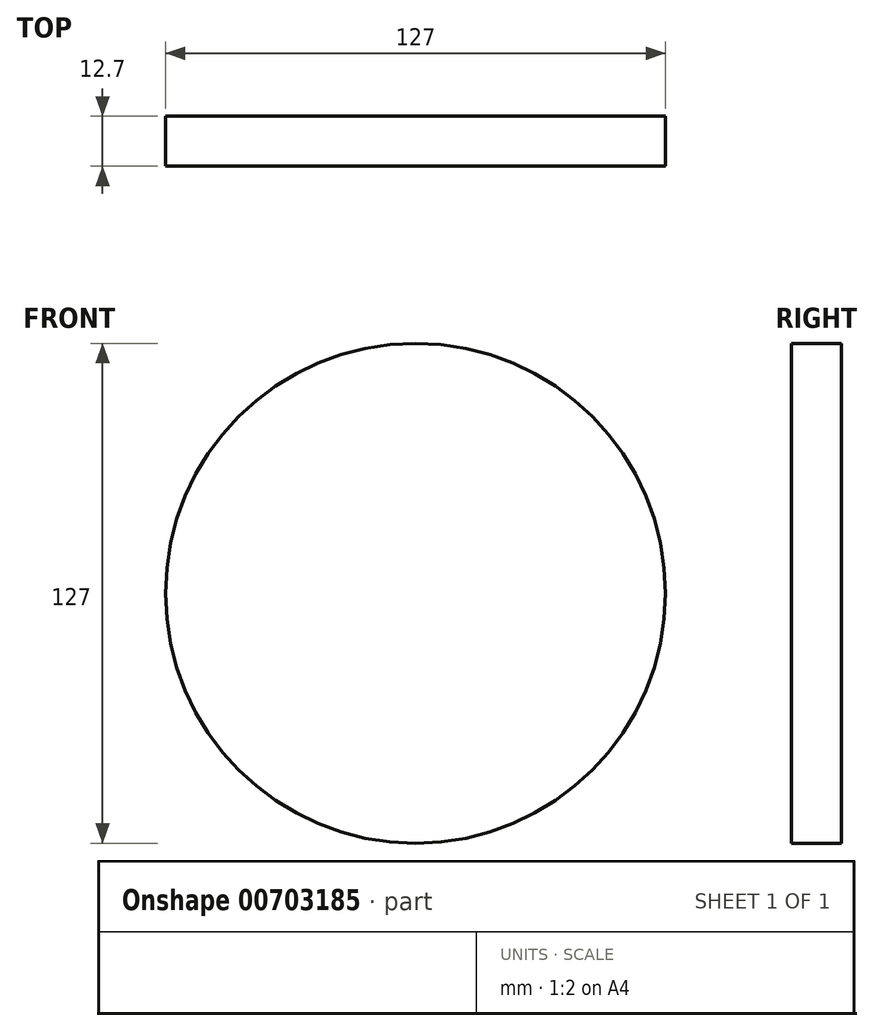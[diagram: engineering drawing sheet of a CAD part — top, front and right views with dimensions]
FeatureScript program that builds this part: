
annotation { "Feature Type Name" : "Feature", "Feature Type Description" : "" }
export const myFeature = defineFeature(function(context is Context, id is Id, definition is map)
    precondition{}
    {
        {
            var Q0;
            Q0=qCreatedBy(makeId("Front.planeOp"),FACE);
            var sketch = newSketch(context, id + "F0", { "sketchPlane" : qUnion([Q0])});
            skCircle(sketch, "E0", {"center": v(0, 0) * mm, "radius": 63.5 * mm});
            skSolve(sketch);
        }
        {
            var Q0;
            Q0=makeQuery(id+"F0.imprint","IMPRINT",FACE,{"disambiguationData":[TD([[makeQuery(id+"F0.imprint","IMPRINT",EDGE,{"derivedFrom":sQuery(id+"F0.wireOp",EDGE,"E0")}),1.0]])]});
            extrude(context, id + "F1", {"entities" : qUnion([Q0]), "depth" : 12.7 * mm, "offsetDistance" : 25.4 * mm});
        }
    });
